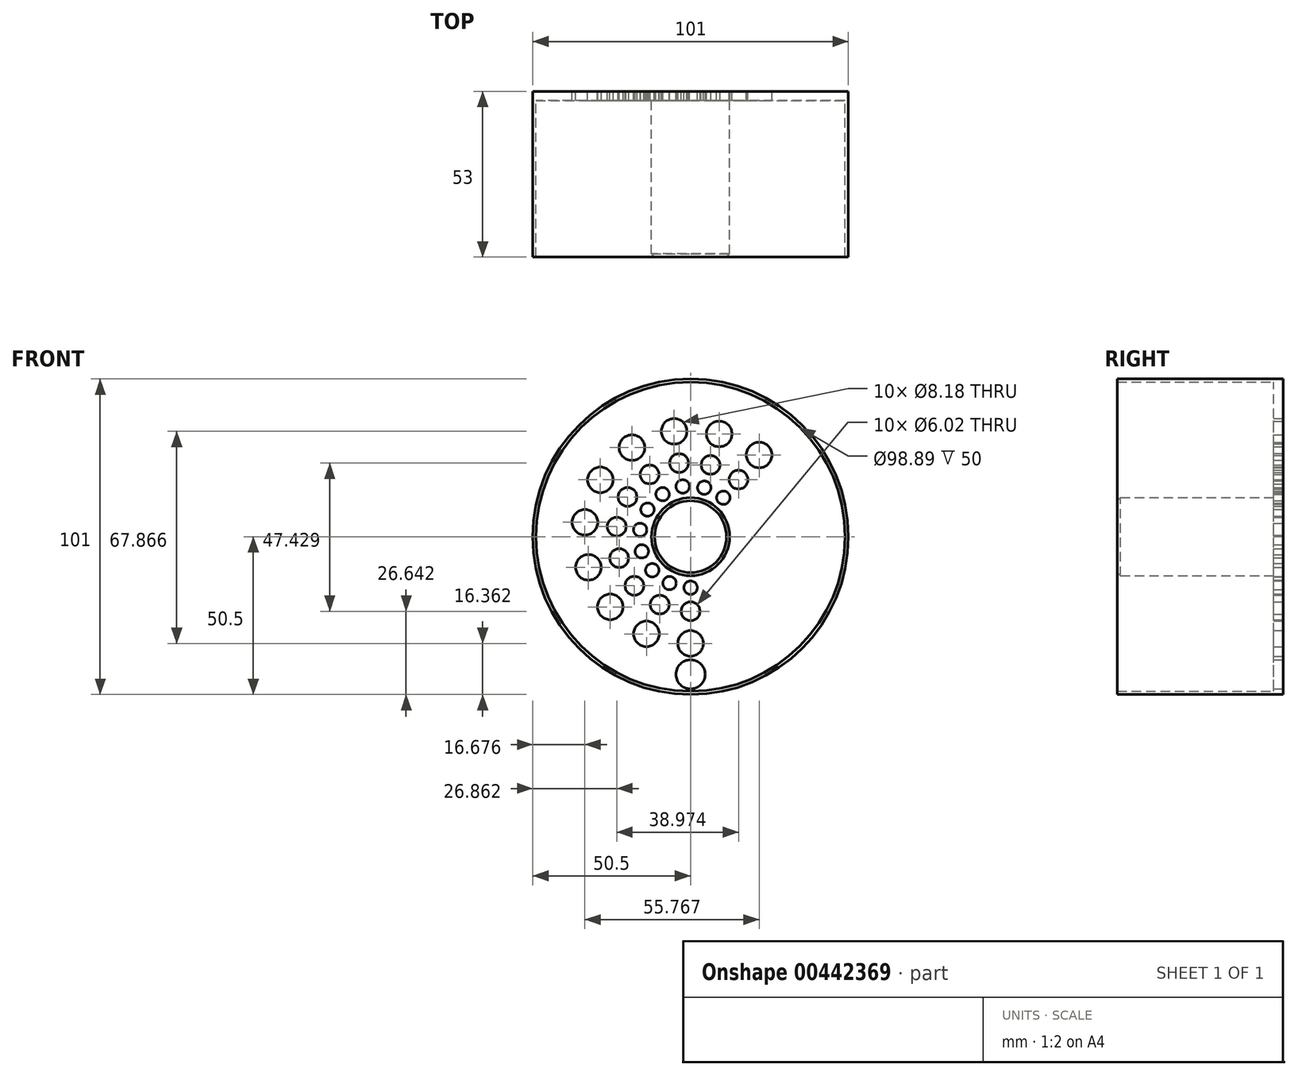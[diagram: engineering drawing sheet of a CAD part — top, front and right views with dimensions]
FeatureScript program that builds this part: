
annotation { "Feature Type Name" : "Feature", "Feature Type Description" : "" }
export const myFeature = defineFeature(function(context is Context, id is Id, definition is map)
    precondition{}
    {
        {
            var Q0;
            Q0=qCreatedBy(makeId("Front.planeOp"),FACE);
            var sketch = newSketch(context, id + "F0", { "sketchPlane" : qUnion([Q0])});
            skCircle(sketch, "E0", {"center": v(0, 0) * mm, "radius": 50.5 * mm});
            skSolve(sketch);
        }
        {
            var Q0;
            Q0=makeQuery(id+"F0.imprint","IMPRINT",FACE,{"disambiguationData":[TD([[makeQuery(id+"F0.imprint","IMPRINT",EDGE,{"derivedFrom":sQuery(id+"F0.wireOp",EDGE,"E0")}),1.0]])]});
            extrude(context, id + "F1", {"entities" : qUnion([Q0]), "depth" : 3 * mm});
        }
        {
            var Q0;
            Q0=makeQuery(id+"F1.opExtrude","CAP_FACE",FACE,{"disambiguationData":[OSD([sQuery(id+"F0.wireOp",EDGE,"E0")])],"isStart":false});
            var sketch = newSketch(context, id + "F2", { "sketchPlane" : qUnion([Q0])});
            skCircle(sketch, "E1", {"center": v(0, 0) * mm, "radius": 49.44 * mm});
            skSolve(sketch);
        }
        {
            var Q0;
            Q0=makeQuery(id+"F2.imprint","IMPRINT",FACE,{"disambiguationData":[TD([[makeQuery(id+"F2.imprint","IMPRINT",EDGE,{"derivedFrom":sQuery(id+"F2.wireOp",EDGE,"E1")}),-1.0]])]});
            extrude(context, id + "F3", {"entities" : qUnion([Q0]), "operationType" : NewBodyOperationType.ADD, "depth" : 50 * mm});
        }
        {
            var Q0;
            Q0=makeQuery(id+"F1.opExtrude","CAP_FACE",FACE,{"disambiguationData":[OSD([sQuery(id+"F0.wireOp",EDGE,"E0")])],"isStart":false});
            var sketch = newSketch(context, id + "F4", { "sketchPlane" : qUnion([Q0])});
            skCircle(sketch, "E2", {"center": v(0, 0) * mm, "radius": 12.5 * mm});
            skSolve(sketch);
        }
        {
            var Q0;
            Q0=makeQuery(id+"F4.imprint","IMPRINT",FACE,{"disambiguationData":[TD([[makeQuery(id+"F4.imprint","IMPRINT",EDGE,{"derivedFrom":sQuery(id+"F4.wireOp",EDGE,"E2")}),1.0]])]});
            extrude(context, id + "F5", {"entities" : qUnion([Q0]), "operationType" : NewBodyOperationType.ADD, "depth" : 50 * mm});
        }
        {
            var Q0;
            Q0=makeQuery(id+"F5.opExtrude","CAP_FACE",FACE,{"disambiguationData":[OSD([sQuery(id+"F4.wireOp",EDGE,"E2")])],"isStart":false});
            chamfer(context, id + "F6", {"entities" : qUnion([Q0]), "width" : 1 * mm, "tangentPropagation" : true});
        }
        {
            var Q0;
            Q0=makeQuery(id+"F1.opExtrude","CAP_FACE",FACE,{"disambiguationData":[OSD([sQuery(id+"F0.wireOp",EDGE,"E0")])],"isStart":true});
            var sketch = newSketch(context, id + "F7", { "sketchPlane" : qUnion([Q0])});
            skLineSegment(sketch, "E3", {"start": v(0, 0) * mm, "end": v(0, -33.68) * mm});
            skSolve(sketch);
        }
        {
            var Q0;
            Q0=makeQuery(id+"F7.imprint","IMPRINT",FACE,{"disambiguationData":[TD([[makeQuery(id+"F7.imprint","IMPRINT",EDGE,{"derivedFrom":makeQuery(id+"F1.opExtrude","CAP_EDGE",EDGE,{"disambiguationData":[OSD([sQuery(id+"F0.wireOp",EDGE,"E0")])],"isStart":true})}),-1.0]])]});
            var sketch = newSketch(context, id + "F8", { "sketchPlane" : qUnion([Q0])});
            skSolve(sketch);
        }
        {
            var Q0;
            Q0=makeQuery(id+"F8.imprint","IMPRINT",FACE,{"disambiguationData":[TD([[makeQuery(id+"F8.imprint","IMPRINT",EDGE,{"derivedFrom":makeQuery(id+"F7.imprint","IMPRINT",EDGE,{"derivedFrom":makeQuery(id+"F1.opExtrude","CAP_EDGE",EDGE,{"disambiguationData":[OSD([sQuery(id+"F0.wireOp",EDGE,"E0")])],"isStart":true})})}),-1.0]])]});
            var sketch = newSketch(context, id + "F9", { "sketchPlane" : qUnion([Q0])});
            skCircle(sketch, "E4", {"center": v(0, -44.03) * mm, "radius": 4.66 * mm});
            skSolve(sketch);
        }
        {
            var Q0;
            Q0=makeQuery(id+"F9.imprint","IMPRINT",FACE,{"disambiguationData":[TD([[makeQuery(id+"F9.imprint","IMPRINT",EDGE,{"derivedFrom":sQuery(id+"F9.wireOp",EDGE,"E4")}),1.0]])]});
            var Q1;
            Q1=sQuery(id+"F9.wireOp",EDGE,"E4");
            extrude(context, id + "F10", {"entities" : qUnion([Q0]), "operationType" : NewBodyOperationType.REMOVE, "surfaceEntities" : qUnion([Q1]), "endBound" : BoundingType.THROUGH_ALL, "oppositeDirection" : true, "depth" : 25 * mm});
        }
        {
            var Q0;
            Q0=makeQuery(id+"F8.imprint","IMPRINT",FACE,{"disambiguationData":[TD([[makeQuery(id+"F8.imprint","IMPRINT",EDGE,{"derivedFrom":makeQuery(id+"F7.imprint","IMPRINT",EDGE,{"derivedFrom":makeQuery(id+"F1.opExtrude","CAP_EDGE",EDGE,{"disambiguationData":[OSD([sQuery(id+"F0.wireOp",EDGE,"E0")])],"isStart":true})})}),-1.0]])]});
            var sketch = newSketch(context, id + "F11", { "sketchPlane" : qUnion([Q0])});
            skCircle(sketch, "E5", {"center": v(0, -34.14) * mm, "radius": 4.1 * mm});
            skCircle(sketch, "E6", {"center": v(0, -23.86) * mm, "radius": 3.01 * mm});
            skCircle(sketch, "E7", {"center": v(0, -16.3) * mm, "radius": 2.14 * mm});
            skCircle(sketch, "E8.1.0", {"center": v(14.13, -31.08) * mm, "radius": 4.1 * mm});
            skCircle(sketch, "E8.2.0", {"center": v(25.72, -22.45) * mm, "radius": 4.1 * mm});
            skCircle(sketch, "E8.3.0", {"center": v(32.7, -9.8) * mm, "radius": 4.1 * mm});
            skCircle(sketch, "E8.4.0", {"center": v(33.82, 4.62) * mm, "radius": 4.1 * mm});
            skCircle(sketch, "E8.5.0", {"center": v(28.88, 18.2) * mm, "radius": 4.1 * mm});
            skCircle(sketch, "E8.6.0", {"center": v(18.76, 28.52) * mm, "radius": 4.1 * mm});
            skCircle(sketch, "E8.7.0", {"center": v(5.27, 33.73) * mm, "radius": 4.1 * mm});
            skCircle(sketch, "E8.8.0", {"center": v(-9.15, 32.89) * mm, "radius": 4.1 * mm});
            skCircle(sketch, "E8.9.0", {"center": v(-21.94, 26.15) * mm, "radius": 4.1 * mm});
            skPoint(sketch, "E8.center", {"position": v(0, 0) * mm});
            skLineSegment(sketch, "E8.anchor1", {"start": v(0, 0) * mm, "end": v(0, -34.14) * mm, "construction": true});
            skLineSegment(sketch, "E8.anchor2", {"start": v(0, 0) * mm, "end": v(-21.94, 26.15) * mm, "construction": true});
            skCircle(sketch, "E9.1.0", {"center": v(9.87, -21.72) * mm, "radius": 3.01 * mm});
            skCircle(sketch, "E9.2.0", {"center": v(17.98, -15.69) * mm, "radius": 3.01 * mm});
            skCircle(sketch, "E9.3.0", {"center": v(22.86, -6.84) * mm, "radius": 3.01 * mm});
            skCircle(sketch, "E9.4.0", {"center": v(23.64, 3.23) * mm, "radius": 3.01 * mm});
            skCircle(sketch, "E9.5.0", {"center": v(20.18, 12.72) * mm, "radius": 3.01 * mm});
            skCircle(sketch, "E9.6.0", {"center": v(13.11, 19.93) * mm, "radius": 3.01 * mm});
            skCircle(sketch, "E9.7.0", {"center": v(3.69, 23.57) * mm, "radius": 3.01 * mm});
            skCircle(sketch, "E9.8.0", {"center": v(-6.4, 22.98) * mm, "radius": 3.01 * mm});
            skCircle(sketch, "E9.9.0", {"center": v(-15.34, 18.28) * mm, "radius": 3.01 * mm});
            skLineSegment(sketch, "E9.anchor1", {"start": v(0, 0) * mm, "end": v(0, -23.86) * mm, "construction": true});
            skLineSegment(sketch, "E9.anchor2", {"start": v(0, 0) * mm, "end": v(-15.34, 18.28) * mm, "construction": true});
            skCircle(sketch, "E10.1.0", {"center": v(6.74, -14.83) * mm, "radius": 2.14 * mm});
            skCircle(sketch, "E10.2.0", {"center": v(12.28, -10.71) * mm, "radius": 2.14 * mm});
            skCircle(sketch, "E10.3.0", {"center": v(15.6, -4.67) * mm, "radius": 2.14 * mm});
            skCircle(sketch, "E10.4.0", {"center": v(16.14, 2.2) * mm, "radius": 2.14 * mm});
            skCircle(sketch, "E10.5.0", {"center": v(13.78, 8.69) * mm, "radius": 2.14 * mm});
            skCircle(sketch, "E10.6.0", {"center": v(8.95, 13.61) * mm, "radius": 2.14 * mm});
            skCircle(sketch, "E10.7.0", {"center": v(2.52, 16.1) * mm, "radius": 2.14 * mm});
            skCircle(sketch, "E10.8.0", {"center": v(-4.37, 15.7) * mm, "radius": 2.14 * mm});
            skCircle(sketch, "E10.9.0", {"center": v(-10.47, 12.48) * mm, "radius": 2.14 * mm});
            skLineSegment(sketch, "E10.anchor1", {"start": v(0, 0) * mm, "end": v(0, -16.3) * mm, "construction": true});
            skLineSegment(sketch, "E10.anchor2", {"start": v(0, 0) * mm, "end": v(-10.47, 12.48) * mm, "construction": true});
            skSolve(sketch);
        }
        {
            var Q0;
            Q0=makeQuery(id+"F11.imprint","IMPRINT",FACE,{"disambiguationData":[TD([[makeQuery(id+"F11.imprint","IMPRINT",EDGE,{"derivedFrom":sQuery(id+"F11.wireOp",EDGE,"E8.8.0")}),1.0]])]});
            var Q1;
            Q1=makeQuery(id+"F11.imprint","IMPRINT",FACE,{"disambiguationData":[TD([[makeQuery(id+"F11.imprint","IMPRINT",EDGE,{"derivedFrom":sQuery(id+"F11.wireOp",EDGE,"E9.8.0")}),1.0]])]});
            var Q2;
            Q2=makeQuery(id+"F11.imprint","IMPRINT",FACE,{"disambiguationData":[TD([[makeQuery(id+"F11.imprint","IMPRINT",EDGE,{"derivedFrom":sQuery(id+"F11.wireOp",EDGE,"E10.8.0")}),1.0]])]});
            var Q3;
            Q3=makeQuery(id+"F11.imprint","IMPRINT",FACE,{"disambiguationData":[TD([[makeQuery(id+"F11.imprint","IMPRINT",EDGE,{"derivedFrom":sQuery(id+"F11.wireOp",EDGE,"E10.9.0")}),1.0]])]});
            var Q4;
            Q4=makeQuery(id+"F11.imprint","IMPRINT",FACE,{"disambiguationData":[TD([[makeQuery(id+"F11.imprint","IMPRINT",EDGE,{"derivedFrom":sQuery(id+"F11.wireOp",EDGE,"E9.9.0")}),1.0]])]});
            var Q5;
            Q5=makeQuery(id+"F11.imprint","IMPRINT",FACE,{"disambiguationData":[TD([[makeQuery(id+"F11.imprint","IMPRINT",EDGE,{"derivedFrom":sQuery(id+"F11.wireOp",EDGE,"E8.9.0")}),1.0]])]});
            var Q6;
            Q6=makeQuery(id+"F11.imprint","IMPRINT",FACE,{"disambiguationData":[TD([[makeQuery(id+"F11.imprint","IMPRINT",EDGE,{"derivedFrom":sQuery(id+"F11.wireOp",EDGE,"E8.7.0")}),1.0]])]});
            var Q7;
            Q7=makeQuery(id+"F11.imprint","IMPRINT",FACE,{"disambiguationData":[TD([[makeQuery(id+"F11.imprint","IMPRINT",EDGE,{"derivedFrom":sQuery(id+"F11.wireOp",EDGE,"E9.7.0")}),1.0]])]});
            var Q8;
            Q8=makeQuery(id+"F11.imprint","IMPRINT",FACE,{"disambiguationData":[TD([[makeQuery(id+"F11.imprint","IMPRINT",EDGE,{"derivedFrom":sQuery(id+"F11.wireOp",EDGE,"E10.7.0")}),1.0]])]});
            var Q9;
            Q9=makeQuery(id+"F11.imprint","IMPRINT",FACE,{"disambiguationData":[TD([[makeQuery(id+"F11.imprint","IMPRINT",EDGE,{"derivedFrom":sQuery(id+"F11.wireOp",EDGE,"E8.6.0")}),1.0]])]});
            var Q10;
            Q10=makeQuery(id+"F11.imprint","IMPRINT",FACE,{"disambiguationData":[TD([[makeQuery(id+"F11.imprint","IMPRINT",EDGE,{"derivedFrom":sQuery(id+"F11.wireOp",EDGE,"E9.6.0")}),1.0]])]});
            var Q11;
            Q11=makeQuery(id+"F11.imprint","IMPRINT",FACE,{"disambiguationData":[TD([[makeQuery(id+"F11.imprint","IMPRINT",EDGE,{"derivedFrom":sQuery(id+"F11.wireOp",EDGE,"E10.6.0")}),1.0]])]});
            var Q12;
            Q12=makeQuery(id+"F11.imprint","IMPRINT",FACE,{"disambiguationData":[TD([[makeQuery(id+"F11.imprint","IMPRINT",EDGE,{"derivedFrom":sQuery(id+"F11.wireOp",EDGE,"E8.5.0")}),1.0]])]});
            var Q13;
            Q13=makeQuery(id+"F11.imprint","IMPRINT",FACE,{"disambiguationData":[TD([[makeQuery(id+"F11.imprint","IMPRINT",EDGE,{"derivedFrom":sQuery(id+"F11.wireOp",EDGE,"E9.5.0")}),1.0]])]});
            var Q14;
            Q14=makeQuery(id+"F11.imprint","IMPRINT",FACE,{"disambiguationData":[TD([[makeQuery(id+"F11.imprint","IMPRINT",EDGE,{"derivedFrom":sQuery(id+"F11.wireOp",EDGE,"E10.5.0")}),1.0]])]});
            var Q15;
            Q15=makeQuery(id+"F11.imprint","IMPRINT",FACE,{"disambiguationData":[TD([[makeQuery(id+"F11.imprint","IMPRINT",EDGE,{"derivedFrom":sQuery(id+"F11.wireOp",EDGE,"E8.4.0")}),1.0]])]});
            var Q16;
            Q16=makeQuery(id+"F11.imprint","IMPRINT",FACE,{"disambiguationData":[TD([[makeQuery(id+"F11.imprint","IMPRINT",EDGE,{"derivedFrom":sQuery(id+"F11.wireOp",EDGE,"E8.2.0")}),1.0]])]});
            var Q17;
            Q17=makeQuery(id+"F11.imprint","IMPRINT",FACE,{"disambiguationData":[TD([[makeQuery(id+"F11.imprint","IMPRINT",EDGE,{"derivedFrom":sQuery(id+"F11.wireOp",EDGE,"E9.2.0")}),1.0]])]});
            var Q18;
            Q18=makeQuery(id+"F11.imprint","IMPRINT",FACE,{"disambiguationData":[TD([[makeQuery(id+"F11.imprint","IMPRINT",EDGE,{"derivedFrom":sQuery(id+"F11.wireOp",EDGE,"E8.3.0")}),1.0]])]});
            var Q19;
            Q19=makeQuery(id+"F11.imprint","IMPRINT",FACE,{"disambiguationData":[TD([[makeQuery(id+"F11.imprint","IMPRINT",EDGE,{"derivedFrom":sQuery(id+"F11.wireOp",EDGE,"E9.3.0")}),1.0]])]});
            var Q20;
            Q20=makeQuery(id+"F11.imprint","IMPRINT",FACE,{"disambiguationData":[TD([[makeQuery(id+"F11.imprint","IMPRINT",EDGE,{"derivedFrom":sQuery(id+"F11.wireOp",EDGE,"E8.1.0")}),1.0]])]});
            var Q21;
            Q21=makeQuery(id+"F11.imprint","IMPRINT",FACE,{"disambiguationData":[TD([[makeQuery(id+"F11.imprint","IMPRINT",EDGE,{"derivedFrom":sQuery(id+"F11.wireOp",EDGE,"E5")}),1.0]])]});
            var Q22;
            Q22=makeQuery(id+"F11.imprint","IMPRINT",FACE,{"disambiguationData":[TD([[makeQuery(id+"F11.imprint","IMPRINT",EDGE,{"derivedFrom":sQuery(id+"F11.wireOp",EDGE,"E6")}),1.0]])]});
            var Q23;
            Q23=makeQuery(id+"F11.imprint","IMPRINT",FACE,{"disambiguationData":[TD([[makeQuery(id+"F11.imprint","IMPRINT",EDGE,{"derivedFrom":sQuery(id+"F11.wireOp",EDGE,"E9.1.0")}),1.0]])]});
            var Q24;
            Q24=makeQuery(id+"F11.imprint","IMPRINT",FACE,{"disambiguationData":[TD([[makeQuery(id+"F11.imprint","IMPRINT",EDGE,{"derivedFrom":sQuery(id+"F11.wireOp",EDGE,"E7")}),1.0]])]});
            var Q25;
            Q25=makeQuery(id+"F11.imprint","IMPRINT",FACE,{"disambiguationData":[TD([[makeQuery(id+"F11.imprint","IMPRINT",EDGE,{"derivedFrom":sQuery(id+"F11.wireOp",EDGE,"E10.1.0")}),1.0]])]});
            var Q26;
            Q26=makeQuery(id+"F11.imprint","IMPRINT",FACE,{"disambiguationData":[TD([[makeQuery(id+"F11.imprint","IMPRINT",EDGE,{"derivedFrom":sQuery(id+"F11.wireOp",EDGE,"E10.2.0")}),1.0]])]});
            var Q27;
            Q27=makeQuery(id+"F11.imprint","IMPRINT",FACE,{"disambiguationData":[TD([[makeQuery(id+"F11.imprint","IMPRINT",EDGE,{"derivedFrom":sQuery(id+"F11.wireOp",EDGE,"E10.3.0")}),1.0]])]});
            var Q28;
            Q28=makeQuery(id+"F11.imprint","IMPRINT",FACE,{"disambiguationData":[TD([[makeQuery(id+"F11.imprint","IMPRINT",EDGE,{"derivedFrom":sQuery(id+"F11.wireOp",EDGE,"E9.4.0")}),1.0]])]});
            var Q29;
            Q29=makeQuery(id+"F11.imprint","IMPRINT",FACE,{"disambiguationData":[TD([[makeQuery(id+"F11.imprint","IMPRINT",EDGE,{"derivedFrom":sQuery(id+"F11.wireOp",EDGE,"E10.4.0")}),1.0]])]});
            extrude(context, id + "F12", {"entities" : qUnion([Q0, Q1, Q2, Q3, Q4, Q5, Q6, Q7, Q8, Q9, Q10, Q11, Q12, Q13, Q14, Q15, Q16, Q17, Q18, Q19, Q20, Q21, Q22, Q23, Q24, Q25, Q26, Q27, Q28, Q29]), "operationType" : NewBodyOperationType.REMOVE, "endBound" : BoundingType.THROUGH_ALL, "oppositeDirection" : true, "depth" : 25 * mm, "offsetDistance" : 25 * mm});
        }
    });
